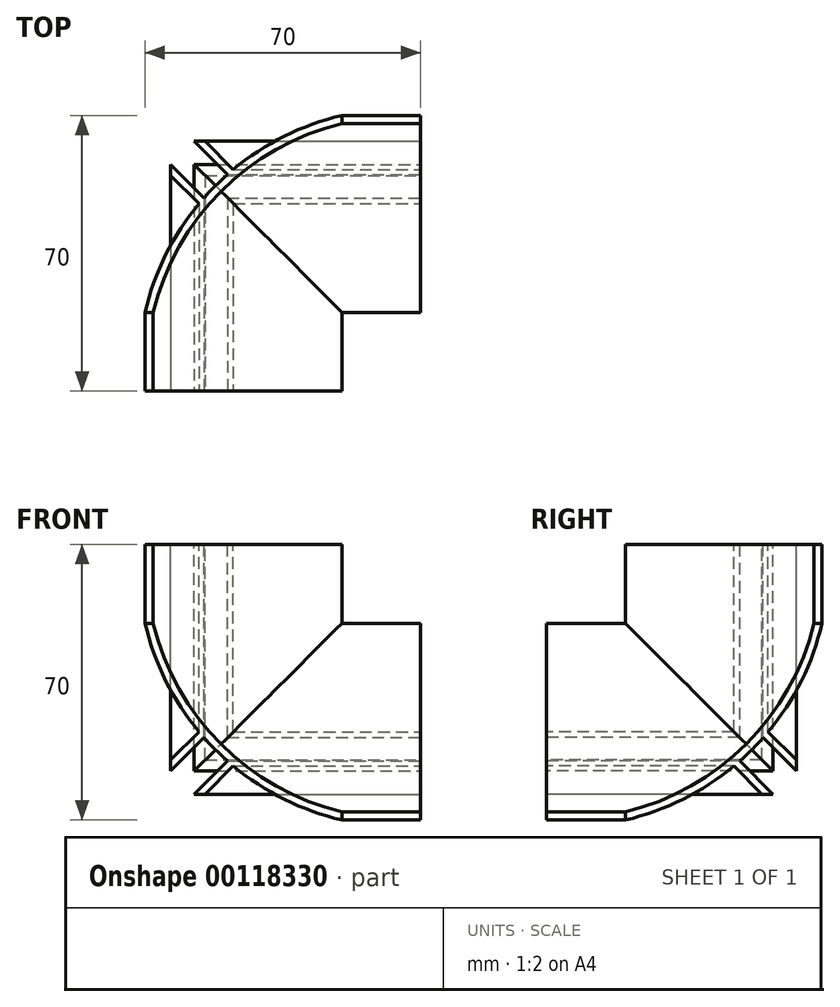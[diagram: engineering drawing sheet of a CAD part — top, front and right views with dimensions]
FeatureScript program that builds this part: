
annotation { "Feature Type Name" : "Feature", "Feature Type Description" : "" }
export const myFeature = defineFeature(function(context is Context, id is Id, definition is map)
    precondition{}
    {
        {
            var Q0;
            Q0=qCreatedBy(makeId("Top.planeOp"),FACE);
            var sketch = newSketch(context, id + "F0", { "sketchPlane" : qUnion([Q0])});
            skLineSegment(sketch, "E0", {"start": v(0, 0) * mm, "end": v(0, -100) * mm});
            skLineSegment(sketch, "E1", {"start": v(0, 0) * mm, "end": v(100, 0) * mm});
            skLineSegment(sketch, "E2", {"start": v(0, 0) * mm, "end": v(-100, 0) * mm});
            skLineSegment(sketch, "E3", {"start": v(0, 0) * mm, "end": v(0, 100) * mm});
            skLineSegment(sketch, "E4", {"start": v(0, 0) * mm, "end": v(0, 50) * mm});
            skLineSegment(sketch, "E5", {"start": v(0, 50) * mm, "end": v(100, 50) * mm});
            skLineSegment(sketch, "E6", {"start": v(100, 50) * mm, "end": v(100, 0) * mm});
            skLineSegment(sketch, "E7", {"start": v(0, 0) * mm, "end": v(-50, 0) * mm});
            skLineSegment(sketch, "E8", {"start": v(-50, 0) * mm, "end": v(-50, -100) * mm});
            skLineSegment(sketch, "E9", {"start": v(-50, -100) * mm, "end": v(0, -100) * mm});
            skLineSegment(sketch, "E10", {"start": v(0, 0) * mm, "end": v(64.97, -64.97) * mm});
            skLineSegment(sketch, "E11", {"start": v(0, 0) * mm, "end": v(-64.84, 64.84) * mm});
            skLineSegment(sketch, "E12", {"start": v(0, 50) * mm, "end": v(20, 50) * mm});
            skLineSegment(sketch, "E13", {"start": v(20, 50) * mm, "end": v(20, 0) * mm});
            skLineSegment(sketch, "E14.MirrorCS", {"start": v(-50, -20) * mm, "end": v(0, -20) * mm});
            skSolve(sketch);
        }
        {
            var Q0;
            Q0=sQuery(id+"F0.wireOp",EDGE,"E14.MirrorCS");
            cPlane(context, id + "F1", {"entities" : qUnion([Q0]), "cplaneType" : CPlaneType.LINE_ANGLE, "offset" : 25 * mm, "angle" : 0 * degree, "width" : 150 * mm, "height" : 150 * mm});
        }
        {
            var Q0;
            Q0=qCreatedBy(id+"F1.planeOp",FACE);
            var sketch = newSketch(context, id + "F2", { "sketchPlane" : qUnion([Q0])});
            skLineSegment(sketch, "E15", {"start": v(0, 0) * mm, "end": v(0, 50) * mm});
            skLineSegment(sketch, "E16", {"start": v(0, 50) * mm, "end": v(50, 50) * mm});
            skLineSegment(sketch, "E17", {"start": v(50, 50) * mm, "end": v(50, 0) * mm});
            skLineSegment(sketch, "E18", {"start": v(50, 0) * mm, "end": v(0, 0) * mm});
            skArc(sketch, "E19", {"start": v(0, 0) * mm, "mid": v(32.13, 17.87) * mm, "end": v(50, 50) * mm});
            skPoint(sketch, "E20", {"position": v(32.13, 17.87) * mm});
            skLineSegment(sketch, "E21", {"start": v(32.13, 17.87) * mm, "end": v(40.53, 9.47) * mm});
            skLineSegment(sketch, "E22", {"start": v(40.53, 9.47) * mm, "end": v(37.56, 6.5) * mm});
            skLineSegment(sketch, "E23", {"start": v(37.56, 6.5) * mm, "end": v(29.07, 15) * mm});
            skLineSegment(sketch, "E24.MirrorCS", {"start": v(40.53, 9.47) * mm, "end": v(43.5, 12.44) * mm});
            skLineSegment(sketch, "E25.MirrorCS", {"start": v(43.5, 12.44) * mm, "end": v(35, 20.93) * mm});
            skLineSegment(sketch, "E26", {"start": v(37.56, 6.5) * mm, "end": v(34.73, 6.5) * mm});
            skLineSegment(sketch, "E27", {"start": v(34.73, 6.5) * mm, "end": v(27.62, 13.74) * mm});
            skLineSegment(sketch, "E28", {"start": v(32.13, 17.87) * mm, "end": v(50, 0) * mm});
            skArc(sketch, "E29.0", {"start": v(-0.46, 1.95) * mm, "mid": v(30.72, 19.28) * mm, "end": v(48.05, 50.46) * mm});
            skLineSegment(sketch, "E30.MirrorCS", {"start": v(43.5, 15.27) * mm, "end": v(36.26, 22.38) * mm});
            skLineSegment(sketch, "E31.MirrorCS", {"start": v(43.5, 12.44) * mm, "end": v(43.5, 15.27) * mm});
            skLineSegment(sketch, "E32", {"start": v(32.13, 17.87) * mm, "end": v(30.72, 19.28) * mm});
            skSolve(sketch);
        }
        {
            var Q0;
            Q0=sQuery(id+"F0.wireOp",EDGE,"E13");
            cPlane(context, id + "F3", {"entities" : qUnion([Q0]), "cplaneType" : CPlaneType.LINE_ANGLE, "offset" : 25 * mm, "angle" : 90 * degree, "width" : 150 * mm, "height" : 150 * mm});
        }
        {
            var Q0;
            Q0=qCreatedBy(id+"F3.planeOp",FACE);
            var sketch = newSketch(context, id + "F4", { "sketchPlane" : qUnion([Q0])});
            skLineSegment(sketch, "E33", {"start": v(0, 0) * mm, "end": v(0, 50) * mm});
            skLineSegment(sketch, "E34", {"start": v(0, 50) * mm, "end": v(50, 50) * mm});
            skLineSegment(sketch, "E35", {"start": v(50, 50) * mm, "end": v(50, 0) * mm});
            skLineSegment(sketch, "E36", {"start": v(50, 0) * mm, "end": v(0, 0) * mm});
            skArc(sketch, "E37", {"start": v(0, 0) * mm, "mid": v(32.13, 17.87) * mm, "end": v(50, 50) * mm});
            skPoint(sketch, "E38", {"position": v(32.13, 17.87) * mm});
            skLineSegment(sketch, "E39", {"start": v(32.13, 17.87) * mm, "end": v(40.53, 9.47) * mm});
            skLineSegment(sketch, "E40", {"start": v(40.53, 9.47) * mm, "end": v(37.56, 6.5) * mm});
            skLineSegment(sketch, "E41", {"start": v(37.56, 6.5) * mm, "end": v(29.07, 15) * mm});
            skLineSegment(sketch, "E42.MirrorCS", {"start": v(40.53, 9.47) * mm, "end": v(43.5, 12.44) * mm});
            skLineSegment(sketch, "E43.MirrorCS", {"start": v(43.5, 12.44) * mm, "end": v(35, 20.93) * mm});
            skLineSegment(sketch, "E44", {"start": v(37.56, 6.5) * mm, "end": v(34.73, 6.5) * mm});
            skLineSegment(sketch, "E45", {"start": v(34.73, 6.5) * mm, "end": v(27.62, 13.74) * mm});
            skLineSegment(sketch, "E46", {"start": v(32.13, 17.87) * mm, "end": v(50, 0) * mm});
            skArc(sketch, "E47.0", {"start": v(-0.46, 1.95) * mm, "mid": v(30.72, 19.28) * mm, "end": v(48.05, 50.46) * mm});
            skLineSegment(sketch, "E48.MirrorCS", {"start": v(43.5, 15.27) * mm, "end": v(36.26, 22.38) * mm});
            skLineSegment(sketch, "E49.MirrorCS", {"start": v(43.5, 12.44) * mm, "end": v(43.5, 15.27) * mm});
            skLineSegment(sketch, "E50", {"start": v(32.13, 17.87) * mm, "end": v(30.72, 19.28) * mm});
            skSolve(sketch);
        }
        {
            var Q0;
            Q0=sQuery(id+"F0.wireOp",EDGE,"E11");
            cPlane(context, id + "F5", {"entities" : qUnion([Q0]), "cplaneType" : CPlaneType.LINE_ANGLE, "offset" : 25 * mm, "angle" : 90 * degree, "width" : 150 * mm, "height" : 150 * mm});
        }
        {
            var Q0;
            {var subQ0=sQuery(id+"F4.wireOp",EDGE,"E41");Q0=makeQuery(id+"F4.imprint","IMPRINT",FACE,{"disambiguationData":[TD([[makeQuery(id+"F4.imprint","IMPRINT",EDGE,{"derivedFrom":subQ0}),1.0]])]});}
            var Q1;
            {var subQ2=sQuery(id+"F4.wireOp",EDGE,"E50");Q1=makeQuery(id+"F4.imprint","IMPRINT",FACE,{"disambiguationData":[TD([[makeQuery(id+"F4.imprint","IMPRINT",EDGE,{"derivedFrom":subQ2}),1.0]])]});}
            var Q2;
            Q2=qCreatedBy(id+"F5.planeOp",FACE);
            extrude(context, id + "F6", {"entities" : qUnion([Q0, Q1]), "endBound" : BoundingType.UP_TO_SURFACE, "oppositeDirection" : true, "endBoundEntityFace" : qUnion([Q2]), "depth" : 25 * mm});
        }
        {
            var Q0;
            {var subQ0=sQuery(id+"F2.wireOp",EDGE,"E23");Q0=makeQuery(id+"F2.imprint","IMPRINT",FACE,{"disambiguationData":[TD([[makeQuery(id+"F2.imprint","IMPRINT",EDGE,{"derivedFrom":subQ0}),1.0]])]});}
            var Q1;
            {var subQ5=sQuery(id+"F2.wireOp",EDGE,"E32");Q1=makeQuery(id+"F2.imprint","IMPRINT",FACE,{"disambiguationData":[TD([[makeQuery(id+"F2.imprint","IMPRINT",EDGE,{"derivedFrom":subQ5}),1.0]])]});}
            var Q2;
            Q2=sQuery(id+"F2.wireOp",EDGE,"E27");
            var Q3;
            Q3=qCreatedBy(id+"F5.planeOp",FACE);
            extrude(context, id + "F7", {"entities" : qUnion([Q0, Q1]), "operationType" : NewBodyOperationType.ADD, "surfaceEntities" : qUnion([Q2]), "endBound" : BoundingType.UP_TO_SURFACE, "endBoundEntityFace" : qUnion([Q3]), "depth" : 25 * mm});
        }
        {
            var Q0;
            Q0=sQuery(id+"F0.wireOp",EDGE,"E5");
            cPlane(context, id + "F8", {"entities" : qUnion([Q0]), "cplaneType" : CPlaneType.LINE_ANGLE, "offset" : 25 * mm, "angle" : 0 * degree, "width" : 150 * mm, "height" : 150 * mm});
        }
        {
            var Q0;
            Q0=qCreatedBy(id+"F8.planeOp",FACE);
            var sketch = newSketch(context, id + "F9", { "sketchPlane" : qUnion([Q0])});
            skPoint(sketch, "E51", {"position": v(-100, 0) * mm});
            skPoint(sketch, "E52", {"position": v(0, 0) * mm});
            skLineSegment(sketch, "E53", {"start": v(-100, 0) * mm, "end": v(-100, 50) * mm});
            skLineSegment(sketch, "E54", {"start": v(-100, 50) * mm, "end": v(0, 50) * mm});
            skLineSegment(sketch, "E55", {"start": v(0, 50) * mm, "end": v(0, 0) * mm});
            skLineSegment(sketch, "E56", {"start": v(-100, 0) * mm, "end": v(0, 0) * mm});
            skLineSegment(sketch, "E57", {"start": v(0, 0) * mm, "end": v(50, 0) * mm});
            skLineSegment(sketch, "E58", {"start": v(50, 0) * mm, "end": v(50, 50) * mm});
            skLineSegment(sketch, "E59", {"start": v(50, 50) * mm, "end": v(0, 50) * mm});
            skLineSegment(sketch, "E60", {"start": v(0, 50) * mm, "end": v(50, 0) * mm});
            skSolve(sketch);
        }
        {
            var Q0;
            Q0=sQuery(id+"F9.wireOp",EDGE,"E60");
            cPlane(context, id + "F10", {"entities" : qUnion([Q0]), "cplaneType" : CPlaneType.LINE_ANGLE, "offset" : 25 * mm, "angle" : 90 * degree, "width" : 150 * mm, "height" : 150 * mm});
        }
        {
            var Q0;
            {var subQ0=sQuery(id+"F4.wireOp",EDGE,"E43.MirrorCS");Q0=makeQuery(id+"F4.imprint","IMPRINT",FACE,{"disambiguationData":[TD([[makeQuery(id+"F4.imprint","IMPRINT",EDGE,{"derivedFrom":subQ0}),-1.0]])]});}
            var Q1;
            {var subQ5=sQuery(id+"F4.wireOp",EDGE,"E50");Q1=makeQuery(id+"F4.imprint","IMPRINT",FACE,{"disambiguationData":[TD([[makeQuery(id+"F4.imprint","IMPRINT",EDGE,{"derivedFrom":subQ5}),-1.0]])]});}
            var Q2;
            Q2=qCreatedBy(id+"F10.planeOp",FACE);
            extrude(context, id + "F11", {"entities" : qUnion([Q0, Q1]), "operationType" : NewBodyOperationType.ADD, "endBound" : BoundingType.UP_TO_SURFACE, "oppositeDirection" : true, "endBoundEntityFace" : qUnion([Q2]), "depth" : 25 * mm});
        }
        {
            var Q0;
            Q0=sQuery(id+"F0.wireOp",EDGE,"E8");
            cPlane(context, id + "F12", {"entities" : qUnion([Q0]), "cplaneType" : CPlaneType.LINE_ANGLE, "offset" : 25 * mm, "angle" : 90 * degree, "width" : 150 * mm, "height" : 150 * mm});
        }
        {
            var Q0;
            Q0=qCreatedBy(id+"F12.planeOp",FACE);
            var sketch = newSketch(context, id + "F13", { "sketchPlane" : qUnion([Q0])});
            skPoint(sketch, "E61", {"position": v(-100, 0) * mm});
            skPoint(sketch, "E62", {"position": v(0, 0) * mm});
            skLineSegment(sketch, "E63", {"start": v(-100, 0) * mm, "end": v(-100, 50) * mm});
            skLineSegment(sketch, "E64", {"start": v(-100, 50) * mm, "end": v(0, 50) * mm});
            skLineSegment(sketch, "E65", {"start": v(0, 50) * mm, "end": v(0, 0) * mm});
            skLineSegment(sketch, "E66", {"start": v(-100, 0) * mm, "end": v(0, 0) * mm});
            skLineSegment(sketch, "E67", {"start": v(0, 0) * mm, "end": v(50, 0) * mm});
            skLineSegment(sketch, "E68", {"start": v(50, 0) * mm, "end": v(50, 50) * mm});
            skLineSegment(sketch, "E69", {"start": v(50, 50) * mm, "end": v(0, 50) * mm});
            skLineSegment(sketch, "E70", {"start": v(0, 50) * mm, "end": v(50, 0) * mm});
            skSolve(sketch);
        }
        {
            var Q0;
            Q0=sQuery(id+"F13.wireOp",EDGE,"E70");
            cPlane(context, id + "F14", {"entities" : qUnion([Q0]), "cplaneType" : CPlaneType.LINE_ANGLE, "offset" : 25 * mm, "angle" : 0 * degree, "width" : 150 * mm, "height" : 150 * mm});
        }
        {
            var Q0;
            {var subQ0=sQuery(id+"F2.wireOp",EDGE,"E25.MirrorCS");Q0=makeQuery(id+"F2.imprint","IMPRINT",FACE,{"disambiguationData":[TD([[makeQuery(id+"F2.imprint","IMPRINT",EDGE,{"derivedFrom":subQ0}),-1.0]])]});}
            var Q1;
            {var subQ5=sQuery(id+"F2.wireOp",EDGE,"E32");Q1=makeQuery(id+"F2.imprint","IMPRINT",FACE,{"disambiguationData":[TD([[makeQuery(id+"F2.imprint","IMPRINT",EDGE,{"derivedFrom":subQ5}),-1.0]])]});}
            var Q2;
            Q2=qCreatedBy(id+"F14.planeOp",FACE);
            extrude(context, id + "F15", {"entities" : qUnion([Q0, Q1]), "operationType" : NewBodyOperationType.ADD, "endBound" : BoundingType.UP_TO_SURFACE, "endBoundEntityFace" : qUnion([Q2]), "depth" : 25 * mm});
        }
        {
            var Q0;
            Q0=qCreatedBy(makeId("Top.planeOp"),FACE);
            cPlane(context, id + "F16", {"entities" : qUnion([Q0]), "cplaneType" : CPlaneType.OFFSET, "offset" : 70 * mm, "width" : 150 * mm, "height" : 150 * mm});
        }
        {
            var Q0;
            Q0=qCreatedBy(id+"F16.planeOp",FACE);
            var sketch = newSketch(context, id + "F17", { "sketchPlane" : qUnion([Q0])});
            skLineSegment(sketch, "E71.MirrorCS", {"start": v(-32.13, 32.13) * mm, "end": v(-30.72, 30.72) * mm});
            skLineSegment(sketch, "E72.MirrorCS", {"start": v(-40.53, 40.53) * mm, "end": v(-43.5, 37.56) * mm});
            skLineSegment(sketch, "E73.MirrorCS", {"start": v(-43.5, 37.56) * mm, "end": v(-43.5, 34.73) * mm});
            skLineSegment(sketch, "E74.MirrorCS", {"start": v(-32.13, 32.13) * mm, "end": v(-40.53, 40.53) * mm});
            skPoint(sketch, "E75.MirrorP", {"position": v(-32.13, 32.13) * mm});
            skLineSegment(sketch, "E76.MirrorCS", {"start": v(-50, 0) * mm, "end": v(0, 0) * mm});
            skLineSegment(sketch, "E77.MirrorCS", {"start": v(0, 0) * mm, "end": v(0, 50) * mm});
            skLineSegment(sketch, "E78.MirrorCS", {"start": v(0, 50) * mm, "end": v(-50, 50) * mm});
            skLineSegment(sketch, "E79.MirrorCS", {"start": v(-50, 50) * mm, "end": v(-50, 0) * mm});
            skArc(sketch, "E80.MirrorCS", {"start": v(-50, 0) * mm, "mid": v(-32.13, 32.13) * mm, "end": v(0, 50) * mm});
            skLineSegment(sketch, "E81.MirrorCS", {"start": v(-43.5, 37.56) * mm, "end": v(-35, 29.07) * mm});
            skLineSegment(sketch, "E82.MirrorCS", {"start": v(-43.5, 34.73) * mm, "end": v(-36.26, 27.62) * mm});
            skLineSegment(sketch, "E83.MirrorCS", {"start": v(-32.13, 32.13) * mm, "end": v(-50, 50) * mm});
            skLineSegment(sketch, "E84.MirrorCS", {"start": v(-37.56, 43.5) * mm, "end": v(-29.07, 35) * mm});
            skLineSegment(sketch, "E85.MirrorCS", {"start": v(-40.53, 40.53) * mm, "end": v(-37.56, 43.5) * mm});
            skLineSegment(sketch, "E86.MirrorCS", {"start": v(-37.56, 43.5) * mm, "end": v(-34.73, 43.5) * mm});
            skLineSegment(sketch, "E87.MirrorCS", {"start": v(-34.73, 43.5) * mm, "end": v(-27.62, 36.26) * mm});
            skArc(sketch, "E88.0", {"start": v(-48.05, -0.46) * mm, "mid": v(-30.72, 30.72) * mm, "end": v(0.46, 48.05) * mm});
            skSolve(sketch);
        }
        {
            var Q0;
            {var subQ3=sQuery(id+"F17.wireOp",EDGE,"E71.MirrorCS");Q0=makeQuery(id+"F17.imprint","IMPRINT",FACE,{"disambiguationData":[TD([[makeQuery(id+"F17.imprint","IMPRINT",EDGE,{"derivedFrom":subQ3}),1.0]])]});}
            var Q1;
            {var subQ0=sQuery(id+"F17.wireOp",EDGE,"E84.MirrorCS");Q1=makeQuery(id+"F17.imprint","IMPRINT",FACE,{"disambiguationData":[TD([[makeQuery(id+"F17.imprint","IMPRINT",EDGE,{"derivedFrom":subQ0}),1.0]])]});}
            var Q2;
            Q2=makeQuery(id+"F17.imprint","IMPRINT",FACE,{"disambiguationData":[TD([[makeQuery(id+"F17.imprint","IMPRINT",EDGE,{"derivedFrom":sQuery(id+"F17.wireOp",EDGE,"E73.MirrorCS")}),1.0]])]});
            var Q3;
            {var subQ7=sQuery(id+"F17.wireOp",EDGE,"E71.MirrorCS");Q3=makeQuery(id+"F17.imprint","IMPRINT",FACE,{"disambiguationData":[TD([[makeQuery(id+"F17.imprint","IMPRINT",EDGE,{"derivedFrom":subQ7}),-1.0]])]});}
            extrude(context, id + "F18", {"entities" : qUnion([Q0, Q1, Q2, Q3]), "operationType" : NewBodyOperationType.ADD, "endBound" : BoundingType.UP_TO_NEXT, "oppositeDirection" : true, "depth" : 25 * mm});
        }
    });
